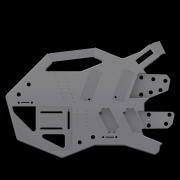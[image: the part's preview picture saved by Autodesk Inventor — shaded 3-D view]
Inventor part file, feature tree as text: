
AUTODESK INVENTOR PART (.ipt)
format: ipt  version: 2020 (Build 240168000, 168)  size: 9,539,584 bytes
history: native  units: in
note: dims shown in document units (in); Inventor stores cm internally (conversion verified against a paired STEP export)
features: other x166, extrude x71, fillet x44, projected_geometry x9, sketch x6, hole x4, loft x3, reference x2, plane x1, move_body x1
ambient origin geometry x8: Origin, YZ Plane, XZ Plane, XY Plane, X Axis, Y Axis, Z Axis, Center Point
bodies: Body (feature_tree), BodyFeature (feature_tree), BodyCut (feature_tree), BodyCutFeature (feature_tree), BodyCutFilletFeature (feature_tree), BodyCutCombineFeature (feature_tree), BodyCutEdgeFilletFeature (feature_tree), BodyRibFrontFilletsFeature (feature_tree), BodyBackRibFilletsFeature (feature_tree), BodyFretboardFilletsFeature (feature_tree), BodyFrontTopFilletsFeature (feature_tree), BodyFrontBottomFilletsFeature (feature_tree), BodyFrontNeckFilletsFeature (feature_tree), Solid22 (feature_tree), Solid23 (feature_tree), Solid62 (feature_tree), Solid64 (feature_tree), Solid65 (feature_tree), Solid68 (feature_tree), Solid50 (feature_tree), Solid52 (feature_tree), Solid54 (feature_tree), Solid56 (feature_tree), Solid57 (feature_tree), Solid59 (feature_tree)
feature tree (307):
  other  "MainBody"
  extrude  "NeckMountsProfileFeature"  Depth=0.5in TaperAngle=0.0deg
  other  "NeckPlane"
  extrude  "8StringFeature"  Depth=4.5in
  extrude  "6StringFeature"  Depth=1.12in
  extrude  "HornFeature"  Depth=0.6788in
  other  "6StringNeckFeature"
  other  "8StringNeckFeature"
  fillet  "InsideCornerFilletsFeature1/8"  Radius=0.6788in
  fillet  "OutsideFilletsFeature1/2"  Radius=0.125in
  fillet  "NeckMountOutsideFilletsFeature1/4"  Radius=0.5in
  fillet  "TipFilletsFeature1/8"  Radius=0.125in
  fillet  "BottomHornTipFilletFeature1/10"  Radius=0.1in
  fillet  "BottomHornFilletsFeature1/8"  Radius=0.125in
  fillet  "InsideHandleFilletsFeature1/2"  Radius=0.5in
  fillet  "InsideHandleFilletsFeature1/8"  Radius=0.125in
  fillet  "InsideTopHornFilletsFeature1/4"  Radius=0.25in
  fillet  "InsideTopHornFilletsFeature1/2"  Radius=0.5in
  fillet  "InsideBottomHornFilletsFeature1/4"  Radius=0.25in
  other  "PickupsOriginal"
  other  "MiddlePlane"
  other  "PickupsCustom"
  other  "PickupsModified"
  extrude  "TopPickupsIndentFeature"  Depth=0.0515in
  extrude  "BottomPickupsIndentFeature"  Depth=0.05in
  extrude  "TopPickupHolesFeature"  Depth=0.05in
  extrude  "BottomPickupHolesFeature"  Depth=0.05in
  fillet  "PickupIndentFilletsFeature"  Radius=5.7in
  other  "Frets"
  other  "FretsPreview"
  other  "TopHornHandleIndent"
  extrude  "TopHornBodyHandleFeature"  Depth=0.05in
  extrude  "TopHornHornHandleFeature"  Depth=0.05in
  other  "HornSculptFeature"
  other  "TopHornHandleFront"
  extrude  "TopHornHandleFrontFeature"  Depth=0.05in
  extrude  "TopHornHandleFront2Feature"  TaperAngle=45.0deg  [1 undecoded]
  extrude  "TopHornHandleFront3Feature"  TaperAngle=120.0deg  [1 undecoded]
  other  "TopHornHandleBack"
  extrude  "TopHornHandleBackFeature"  Depth=0.05in
  extrude  "TopHornHandleBack2Feature"  Depth=0.05in
  extrude  "TopHandleFeature"  Depth=0.05in
  extrude  "TopHandleFrontFeature"  Depth=0.05in
  extrude  "TopHandleBackFeature"  Depth=0.05in
  other  "Tuners"
  hole  "TunerHolesFeature"  [1 undecoded]
  other  "LogoMount"
  extrude  "LogoMountFeature"  Depth=0.05in
  other  "SideProfile"
  extrude  "SideProfileFeature"  Depth=0.05in
  other  "KeyboardCompartmentSidePlane"
  extrude  "KeyboardCompartmentFeature"  Depth=0.05in
  fillet  "KeyboardCompartmentFilletsFeature"  Radius=1.7in
  other  "ControlsBottom"
  other  "ControlsTop2"
  other  "ControlsTop1"
  extrude  "ControlsTop1Feature"  Depth=0.05in
  extrude  "ControlsTop2Feature"  Depth=0.05in
  extrude  "ControlsBottomFeature"  Depth=0.05in
  other  "HornSculptSideProfileFeature"
  fillet  "HornFretboardFilletFeature"  Radius=1.1in
  other  "ElectronicsCompartments"
  other  "InsideFacePlane1"
  other  "InsideFacePlane2"
  other  "InsideFacePlane3"
  extrude  "ElectronicCompartmentTopFeature"  Depth=0.05in
  extrude  "ElectronicCompartmentBottomFeature"  Depth=0.05in
  other  "ElectronicCompartmentsSculpt1Feature"
  other  "ElectronicCompartmentsSculpt2Feature"
  other  "ElectronicCompartmentsSculpt3Feature"
  other  "ElectronicCompartmentsSubtractFeature"
  extrude  "ElectronicCompartmentsSubtract2Feature"  Depth=0.05in
  fillet  "ElectronicCompartmentFillets1Feature"  Radius=1.277in
  fillet  "ElectronicCompartmentFillets2Feature"  Radius=1.277in
  extrude  "ControlIndentsBottomFeature"  Depth=0.05in
  fillet  "ElectronicCompartmentFillets3Feature"  Radius=1.0857in
  fillet  "ElectronicCompartmentFillets4Feature"  Radius=3.0in
  extrude  "ControlIndentsTopFeature"  Depth=0.05in
  other  "ControlIndents2Top"
  extrude  "ControlIndents2TopFeature"  Depth=0.05in
  fillet  "ControlIndents3FilletsFeature"  Radius=3.3665in
  extrude  "ControlIndents2RecutFeature"  Depth=0.05in
  fillet  "ElectronicCompartmentInsideFilletsFeature"  Radius=2.6in
  other  "BottomBridgePickupWirePlane"
  extrude  "BottomBridgePickupWireHoleFeature"  Depth=0.05in
  other  "BottomNeckPickupWirePlane"
  extrude  "BottomNeckPickupWireFeature"  Depth=0.05in
  extrude  "TopPickupWireFeature"  Depth=0.05in
  other  "SeaboardBlockCircuitboardMounts"
  extrude  "SeaboardBlockMountStemFeature"  Depth=0.05in
  extrude  "SeaboardBlockMountsFeature"  Depth=0.05in
  other  "SeaboardBlockKeyMounts"
  extrude  "SeaboardBlockKeyMountsFeature"  Depth=0.05in
  extrude  "SeaboardBlockRibbonsFeature"  Depth=0.05in
  extrude  "TunersTopFeature"  Depth=0.05in
  extrude  "TunersMiddleFeature"  Depth=0.05in
  extrude  "TunersBottomFeature"  Depth=0.05in
  fillet  "TunerFilletsFeature"  Radius=0.45in
  extrude  "NeckCutFeature"  Depth=0.05in
  fillet  "NeckCutFilletFeature"  Radius=1.481in
  other  "NeckCutCombineFeature"
  fillet  "NeckCutEdgeFilletFeature"  Radius=0.25in
  fillet  "NeckCutCornerFilletsFeature"  Radius=0.25in
  extrude  "NeckMountsFeature"  Depth=0.05in
  extrude  "FretMarkersTopFeature"  Depth=0.05in
  extrude  "FretMarkersBottomFeature"  TaperAngle=0.0deg  [1 undecoded]
  extrude  "FretsPreviewFeature"  Depth=0.3937in
  extrude  "FretLocksPreviewFeature"  Depth=0.05in
  hole  "FretLocksHolesFeature"  [1 undecoded]
  extrude  "TopHornHandleBodyFeature"  Depth=0.05in
  other  "TopHornSculpt3Feature"
  other  "TopHornSculpt4Feature"
  other  "TopHornSculpt5Feature"
  fillet  "TopHornHandleBodyFilletsFeature"  [1 undecoded]
  fillet  "TopHornHandleFilletsFeature"  [1 undecoded]
  other  "TopHornAdjustFeature"
  fillet  "TopHornAdjustFilletFeature"  Radius=26.75in
  other  "HandlePlane1"
  other  "HandlePlane2"
  other  "Handle"
  extrude  "HandleBackFeature"  Depth=0.05in
  extrude  "HandleFrontFeature"  Depth=0.05in
  other  "HandleSculpt1Feature"
  other  "HandleSculpt2Feature"
  other  "HandleSculpt3Feature"
  other  "HandleSculpt4Feature"
  other  "HandleSculpt5Feature"
  other  "HandleSculpt6Feature"
  other  "HandleEdit1Feature"
  other  "HandleEdit2Feature"
  fillet  "HandleBodyFilletsFeature"  Radius=0.3333in
  fillet  "HandleRibFilletsFeature"  Radius=0.333in
  other  "HornBackSculptFeature"
  other  "HornHandleBackSculpt1Feature"
  other  "HornHandleBackSculpt2Feature"
  fillet  "HornHandleackSculptFilletsFeature"  Radius=0.1in
  fillet  "HandleMeshFilletsFeature"  Radius=0.1in
  fillet  "HornMeshFillets1Feature"  [1 undecoded]
  fillet  "FretboardEndFilletsFeature"  Radius=0.1in
  other  "KeyboardCompartmentSideProfile"
  extrude  "KeyboardCompartmentExactFeature"  Depth=0.05in
  extrude  "KeyboardCompartmentSideFeature"  Depth=0.05in
  other  "KeyboardCompartmentExactSubtractFeature"
  other  "8NeckSplitFeature"
  other  "8NeckLoftStartPlane"
  other  "8NeckLoftEndPlane"
  loft  "8NeckLoftFeature"
  other  "6NeckSplitForLoftFeature"
  other  "6NeckLoftEndPlane"
  other  "6NeckLoftStartPlane"
  extrude  "OscScreenFeature"  Depth=0.05in
  other  "OscCompartmentPlane"
  other  "OscIndentPlane"
  extrude  "OscCompartmentFeature"  Depth=0.05in
  other  "OscCompartmentSubtractFeature"
  extrude  "OscMountFeature"  Depth=0.05in
  other  "OscCoverIndentPlane"
  extrude  "OscCoverIndentFeature"  TaperAngle=0.0deg  [1 undecoded]
  fillet  "OscCoverIndentFilletsFeature"  Radius=0.25in
  extrude  "OscCoverMountHolesFeature"  Depth=0.05in TaperAngle=0.0deg
  fillet  "ElectronicCompartmentLastFilletFeature"  Radius=0.2in
  loft  "6NeckLoftFeature"
  extrude  "6CloseCutFeature"  Depth=0.05in
  other  "HeadSculpt1Feature"
  other  "HeadThickness"
  other  "HeadSculpt2Feature"
  other  "HeadSculpt3Plane"
  extrude  "HeadSculpt3Feature"  Depth=0.05in
  other  "HeadSculpt4Feature"
  other  "8HeadCombineFeature"
  other  "8HeadCleanupFeature"
  fillet  "8HeadFilletFeature"  Radius=0.5333in
  other  "HeadSculpt5Plane"
  other  "HeadSculpt5Feature"
  other  "HeadSculpt6Feature"
  other  "HeadSculpt7Plane"
  extrude  "HeadSculpt7Feature"  Depth=0.05in
  other  "6StringCombineFeature"
  other  "6NeckFilletSplitFeature"
  other  "8NeckFilletSplitFeature"
  fillet  "InsideHeadFilletFeature"  Radius=0.5in
  other  "CombineFilletsFeature"
  fillet  "HornHeadFilletsFeature"  Radius=5.55in
  fillet  "HornFillet3Feature"  Radius=1.75in
  other  "HornFinalSplitFeature"
  other  "6FinalSplitFeature"
  other  "6CombineFeature"
  other  "8NeckJoin"
  other  "6NeckJoin"
  extrude  "8NeckJoinFeature"  Depth=0.05in
  fillet  "8NeckJoinFilletFeature"  Radius=0.1in
  extrude  "6NeckJoinFeature"  TaperAngle=0.0deg  [1 undecoded]
  extrude  "SeaboardBlockMountHolesFeature"  Depth=0.05in
  extrude  "PickupRecutFeature"  Depth=0.3937in
  extrude  "BackCoverIndentFeature"  Depth=0.05in
  extrude  "ElectronicsCompartmentSupportFeature"  Depth=0.05in
  fillet  "ElectronicsCompartmentSupportFilletsFeature"  Radius=0.2in
  hole  "BackCoverMountsFeature"  [1 undecoded]
  other  "OscCoverBottom"
  other  "OscCoverTopPlane"
  other  "OscCoverMounts"
  loft  "OscCoverFeature"
  extrude  "OscCoverBodyCutFeature"  Depth=0.05in TaperAngle=0.0deg
  fillet  "OscCoverBodyCutFilletsFeature"  Radius=0.125in
  other  "OscCoverBodyCutSubtractFeature"
  fillet  "OscCoverBodyFilletFeature"  Radius=0.1in
  extrude  "OscCoverMountsFeature"  Depth=0.05in
  extrude  "LogoCompartmentFeature"  Depth=0.05in
  other  "LogoMounts"
  extrude  "LogoMountsFeature"  Depth=0.05in
  fillet  "LogoMountsFilletsFeature"  Radius=0.25in
  hole  "LogoMountHolesFeature"  [1 undecoded]
  extrude  "Extrusion179"  Depth=0.05in
  other  "KeyboardCompartment"
  other  "TopHandle"
  other  "TunerLocksBody"
  other  "FretsBody"
  other  "TunersTop"
  other  "TunersMiddle"
  other  "TunersBottom"
  other  "ElectronicCompartments1Body"
  other  "NeckCut"
  other  "NeckMounts"
  other  "TopHornHandle"
  other  "TopHornHandleBody"
  projected_geometry  "Projected Loop22"
  projected_geometry  "Projected Loop23"
  other  "TopHandleFront"
  projected_geometry  "Projected Loop24"
  other  "TopHandleBack"
  other  "HandleBody"
  other  "TopHornSculpt3Plane"
  other  "TopHornSculpt4Plane"
  other  "TopHornSculpt5Plane"
  other  "HandleSculpt1Plane"
  other  "HandleSculpt2Plane"
  other  "HandleSculpt3Plane"
  other  "HandleSculpt4Plane"
  other  "HandleSculpt5Plane"
  other  "HandleSculpt6Plane"
  other  "HornBody"
  other  "8StringBody"
  other  "6StringBody"
  other  "NeckMountsProfile"
  other  "HornBackSculptPlane"
  other  "HornSculptFrontPlane"
  plane  "Work Plane62"
  other  "8NeckStartProfile"
  other  "8NeckEndProfile"
  sketch  "Sketch127"  dims[d8=0.7696in d18=0.5in d119=1.75in d120=0.0in]
  other  "6NeckLoftStartProfile"
  other  "6NeckLoftEndProfile"
  projected_geometry  "Projected Loop27"
  other  "6CloseCut"
  sketch  "Sketch131"  dims[d433=1.0857in d464=4.5in d466=0.25in]
  other  "HeadSculpt1Plane"
  other  "HeadSculpt2Plane"
  other  "HeadSculpt3Profile"
  other  "HeadSculpt4Plane"
  other  "HeadSculpt7Profile"
  other  "6NeckFilletSplit"
  other  "8NeckFilletSplit"
  sketch  "Sketch138"  dims[d501=0.25in d582=1.12in]
  sketch  "Sketch139"  dims[d644=25.0in d654=0.6788in d681=0.6788in d700=0.125in d702=0.5in d703=0.125in d705=0.1in d706=0.125in d707=0.5in d708=0.125in d709=0.25in d710=0.5in d711=0.25in]
  other  "ControlIndentsBottom"
  other  "BottomBridgePickupWireHole"
  other  "BottomNeckPickupWire"
  other  "TopPickupWire"
  other  "HornHandleBackSculpt1Plane"
  other  "HornHandleBackSculpt2Plane"
  sketch  "Sketch165"  dims[d716=2.2835in d717=0.0515in]
  other  "OscScreen"
  other  "OscCompartment"
  other  "OscMount"
  other  "OscCoverPlane"
  other  "OscCoverIndent"
  other  "OscCoverMountHoles"
  projected_geometry  "Projected Loop32"
  other  "KeyboardCompartmentExact"
  projected_geometry  "Projected Loop35"
  other  "SeaboardBlockMountHoles"
  reference  "Reference6"
  reference  "Reference7"
  other  "PickupRecut"
  other  "BackCoverIndent"
  other  "ElectronicsCompartmentSupport"
  other  "BackCoverMounts"
  other  "OscCoverTop"
  other  "OscCoverBody"
  other  "LogoCompartment"
  sketch  "Sketch206"  dims[d718=13.825in d719=0.213in d721=0.9414in d722=1.1649in d724=5.7in d725=7.5379in d726=0.2542in d727=2.0in d728=45.0deg d729=120.0deg d730=0.3642in d731=0.9371in d745=5.6289in d747=6.0in d748=4.3in d750=0.8658in d751=0.6506in d753=0.4054in d754=0.8in d779=0.101in d781=1.7in d782=7.125in d783=2.6in d784=0.933in d787=1.1in d792=3.625in d793=4.0in d819=3.5in d825=1.277in d834=1.277in d836=1.5in d837=1.0857in d838=3.0in d839=2.0in d841=4.5in d846=3.3665in d850=0.1512in d853=2.6in d864=1.5757in d961=0.5in d962=0.5in d963=0.3779in d964=0.3779in d965=0.45in d966=0.45in d967=0.8795in d968=1.1386in d969=1.1386in d970=0.45in d971=4.009in d972=1.481in d979=0.25in d980=0.25in d982=0.1718in d983=0.1718in d984=0.0in d985=0.7874in d987=4.0in d988=0.3937in d990=1.0in d994=2.746in d995=1.481in d996=0.9256in d999=0.0in d1000=0.0in d1022=26.75in d1023=28.0in d1024=25.5in d1026=0.3333in d1041=0.333in d1042=0.1in d1044=0.1in d1048=0.0in d1049=0.0in d1054=0.1in d1055=0.1in d1057=0.748in d1060=0.0in d1061=0.0in d1064=0.4662in d1092=0.7in d1095=1.7in d1100=0.0in d1101=0.0in d1117=0.25in d1118=0.0in d1119=0.3in d1120=0.0in d1122=0.2in d1123=0.0in d1277=0.6459in d1329=0.5333in d1334=0.333in d1335=0.5333in d1339=0.125in d1348=0.5in d1358=5.55in d1359=1.75in d1373=0.2in d1375=0.1in d1376=0.0in d1406=1.125in d1430=3.1496in d1432=0.525in d1433=0.3937in d1435=1.0in d1439=1.8in d1440=1.125in d1441=0.2in d1475=0.1in d1476=0.75in d1477=0.375in d1478=0.25in d1479=0.5635in d1480=0.5in d1481=0.8108in d1483=0.05in d1484=0.0in d1485=0.05in d1486=0.0in d1487=0.05in d1488=0.0in d1489=0.125in d1490=0.1in d1491=2.846in d1492=1.481in d1493=0.5in d1494=0.25in d1496=0.1in d1504=0.13in d1508=0.1in d1511=3.063in d1512=0.1295in d1513=0.1295in d1526=0.5708in d1527=0.1286in d1528=1.3799in d1529=1.3958in d1530=1.1055in d1531=0.8208in d1534=2.3622in d1536=0.45in d1537=0.3937in d1539=1.0in d1574=1.0in d1575=0.0in d1576=0.0in d1577=0.4789in d1578=0.4308in d1579=1.1471in d1580=2.5in d1581=1.275in d1582=1.1845in d1583=1.481in d1584=1.1384in d1585=0.7644in d1586=2.746in d1587=0.264in d1588=0.4in d1589=0.0in d1590=0.75in d1591=0.0in d1592=1.0in d1593=0.0in d1594=1.0in d1595=0.0in d1596=0.144in d1597=3.75in d1598=0.1295in d1599=0.1295in d1638=10.0in d1639=14.2465in d1641=11.25in d1648=0.5in d1649=0.0in d1650=28.0in d1657=1.0in d1659=5.5in d1660=4.25in d1662=0.3333in d1663=0.0in d1664=10.0in d1665=1.0in d1671=0.1in d1672=0.5in d1676=3.0in d1677=2.425in d1682=0.75in d1683=0.0in d1690=1.1878in d1691=0.9817in d1692=1.0844in d1693=0.8784in d1695=0.2in d1696=0.0in d1750=1.525in d1751=0.0in d1752=0.5in d1777=0.5in d1778=0.0in d1779=0.5in d1780=0.0in d1781=0.5in d1782=0.0in d1783=0.6in d1784=0.0in d1790=0.65in d1791=0.0in d1792=0.65in d1793=0.0in d1795=0.125in d1821=0.1in d1828=0.0in d1829=0.0in d1830=0.475in d1831=0.125in d1832=0.125in d1843=3.0403in d1844=2.1333in d1845=0.758in d1847=1.75in d1848=0.0in d1849=1.9in d1850=0.0in d1851=1.9in d1852=0.0in d1858=0.9in d1859=0.0in d1862=0.0in d1863=0.0in d1864=0.5in d1865=0.0in d1866=0.5in d1867=0.0in d1870=0.2056in d1871=0.257in d1872=0.0674in d1875=0.25in d1876=0.0in d1877=0.15in d1880=0.15in d1882=0.05in d1883=0.05in d1885=1.3537in d1887=10.0in d1888=0.1in d1889=0.1in d1890=20.0in d1891=20.0in d1894=0.0618in d1900=0.1in d1901=0.4524in d1903=0.006in d1904=0.0in d1915=0.22in d1921=0.0in d1922=90.0deg d1923=0.0in d1924=90.0deg d1925=1.2in d1926=0.7in d1927=0.3333in d1928=0.001in d1929=0.25in d1930=1.25in d1931=0.25in d1935=0.8in d1936=0.3489in d1937=0.22in d1938=0.25in d1939=0.5in d1940=0.6in d1941=0.15in d1942=0.4in d1943=0.0in d1944=90.0deg d1945=0.0in d1946=90.0deg d1948=1.3333in d1949=2.125in d1951=1.125in d1952=2.55in d1957=3.0in d1958=0.1in d1959=0.1in d1960=0.1in d1961=1.0in d1962=0.0in d1966=1.0in d1967=0.0in d1968=0.44in d1969=0.0in d1975=0.1in d1976=0.1in d1980=10.6875in d1981=5.1875in d1982=0.85in d1983=0.3333in d1985=7.5816in d1987=0.1in d1988=0.0in d1989=0.1875in d1990=0.5333in d1992=150.0deg d1993=3.25in d1996=-0.325in d1997=-0.125in d1998=1.0in d1999=0.0in d2004=0.5in d2005=0.0in d2007=0.0938in d2008=0.5in d2009=0.25in d2010=2.3125in d2011=0.7188in d2015=0.25in d2016=5.0in d2019=0.125in d2020=0.25in d2027=0.2in d2028=0.0in d2029=0.02in d2030=0.0in d2039=0.55in d2047=0.25in d2048=0.25in d2049=0.0in d2050=0.0in d2052=2.295in d2053=0.0in d2056=0.25in d2058=0.25in d2059=0.3333in d2060=0.3333in d2061=0.25in d2062=0.3333in d2063=0.3333in d2064=0.0in d2065=0.0in d2066=0.339in d2067=0.1643in d2068=0.1in d2069=0.1in d2070=0.1in d2071=0.1in d2072=0.1643in d2073=0.1643in d2074=0.1643in d2077=3.3125in d2078=3.313in d2079=0.305in d2080=0.3333in d2081=1.0in d2082=0.0in d2083=0.3333in d2084=0.0in d2086=0.719in d2087=2.3125in d2088=0.125in d2089=0.1in d2090=0.438in d2091=0.438in d2092=0.438in d2093=0.438in d2094=0.25in d2095=0.0in d2096=0.25in d2097=0.25in d2098=2.0in d2100=2.5in d2102=0.75in d2103=0.25in d2104=0.25in d2105=0.0in d2106=0.625in d2111=10.0in d2112=0.125in d2113=0.3333in d2117=1.75in d2118=1.25in d2119=1.625in d2120=0.25in d2121=1.0in d2122=0.1in d2125=0.7in d2132=1.625in d2133=1.0in d2134=0.1in d2135=1.0in d2136=1.0in d2137=0.1in d2138=1.025in d2139=1.025in d2140=0.5in d2141=0.7in d2142=1.075in d2143=0.7in d2144=0.5in d2146=0.25in d2147=0.25in d2148=0.5in d2149=1.75in d2150=0.0in d2151=0.0in d2152=0.035in d2153=0.0in d2154=0.0in d2155=0.0in d2156=-0.325in d2157=1.0in d2158=0.2in d2159=0.0in d2160=1.0in d2161=0.2in d2162=0.0in d2164=1.0in d2165=2.2612in d2166=0.605in d2167=0.01in d2168=0.3333in d2169=0.5388in d2170=0.4in d2171=2.625in d2172=1.375in d2173=0.172in d2174=0.281in d2175=0.5in d2176=0.0in d2177=-2.0in d2178=1.797in d2179=0.0in d2180=-0.125in d2181=0.06in d2182=0.06in d2183=0.505in d2184=0.9375in d2185=2.625in d2186=1.375in d2187=2.5in d2188=1.0313in d2189=0.05in d2190=0.1719in d2191=0.0625in d2192=0.0625in d2193=0.1094in d2194=0.0312in d2195=0.0312in d2196=0.0312in d2197=0.0312in d2198=0.0312in d2199=0.0312in d2200=0.0312in d2201=0.0312in d2202=0.203in d2203=0.0in d2207=-0.2in d2211=0.15in d2212=1.0in d2213=0.0in d2214=0.15in d2215=0.15in d2216=0.1in d2220=0.05in d2221=1.5in d2222=0.0in d2230=0.6836in d2238=1.0in d2239=0.25in d2240=0.1in d2241=0.0689in d2243=1.1408in d2244=0.449in d2245=1.6223in d2246=2.1038in d2247=0.449in d2248=0.0463in d2249=0.4549in d2251=0.3908in d2252=0.3908in d2255=0.8in d2257=3.5in d2259=1.1973in d2261=0.625in d2262=0.625in d2263=0.536in d2264=2.7in d2265=0.25in d2266=0.2in d2267=0.0in d2268=0.2in d2269=0.0in d2278=0.4264in d2279=1.0in d2280=0.0in d2281=21.986in d2282=0.0in d2283=0.1in d2284=0.1in d2285=0.5in d2286=0.0in d2287=0.5333in d2288=0.1in d2293=0.85in d2294=1.0in d2295=0.25in d2296=0.749in d2297=0.0in d2298=0.25in d2299=0.1984in d2300=0.1in d2301=0.0in d2302=0.2in d2303=0.0in d2304=0.481in d2305=0.481in d2306=0.5in d2307=0.25in d2308=0.1in d2309=0.75in d2310=0.375in d2311=0.25in d2312=0.5635in d2313=0.5in d2314=0.8108in d2319=0.0in d2320=0.0in d2321=90.0deg d2322=0.0in d2323=90.0deg d2324=0.5in d2325=0.0in d2326=28.0in d2327=1.0in d2328=1.5in d2329=0.0in d2330=0.2in d2331=0.2in d2333=0.22in d2335=0.12in d2336=0.12in d2337=0.1in d2338=0.1in d2339=0.75in d2340=0.375in d2341=0.25in d2342=0.5635in d2343=0.5in d2344=0.8108in d2347=0.25in d2348=0.3in d2349=0.15in d2350=0.15in d2351=0.3in d2352=0.15in d2353=0.3in d2354=0.25in d2355=0.25in d2356=0.25in d2357=0.25in d2358=0.25in d2359=0.1958in d2360=0.1958in d2361=0.1in d2362=0.1in d2363=0.1in d2364=0.1in d2365=0.2in d2366=0.0in d2369=0.3333in d2370=0.0in d2371=0.05in d2372=0.05in d2373=0.75in d2374=0.375in d2375=0.25in d2376=0.5635in d2377=1.0in d2378=0.8108in d2379=1.05in d2380=0.0in d2381=0.7in d2382=0.6in d620=0.5in d621=0.0344in d622=0.5in d623=0.0344in d1625=0.5in d1626=0.0344in d1627=0.5in d1628=0.0344in d1730=0.5in d1731=0.0344in d1732=0.5in d1733=0.0344in d1822=0.5in d1823=0.0344in d1824=0.5in d1825=0.0344in d1837=0.5in d1838=0.0344in d1839=0.5in d1840=0.0344in d1860=0.5in d1861=0.0344in d1947=0.5in d1950=0.0344in d2012=0.5in d2013=0.0344in d2101=0.5in]
  projected_geometry  "Projected Loop40"
  projected_geometry  "Projected Loop41"
  projected_geometry  "Projected Loop42"
  other  "Delete13"
  move_body  "Move3"
  other  "Delete14"
  other  "6StringNeckCombineBody"
  other  "8StringNeckBody"
  other  "6StringNeckBody"
  other  "TopHornBody"
  other  "8StringCombinedBody"
  other  "6StringCombinedBody"
  other  "Delete18"
  other  "<userpath>\Desktop\switchback\src\switchback-exploded.iam"
  other  "switchback-exploded.iam"
  other  "seaboard-block-keyboard:1"
note: 12 required parameter values undecoded (feature->parameter linkage not recoverable at this tier; creation-order binding heuristic only, values carry confidence <= 0.55)
